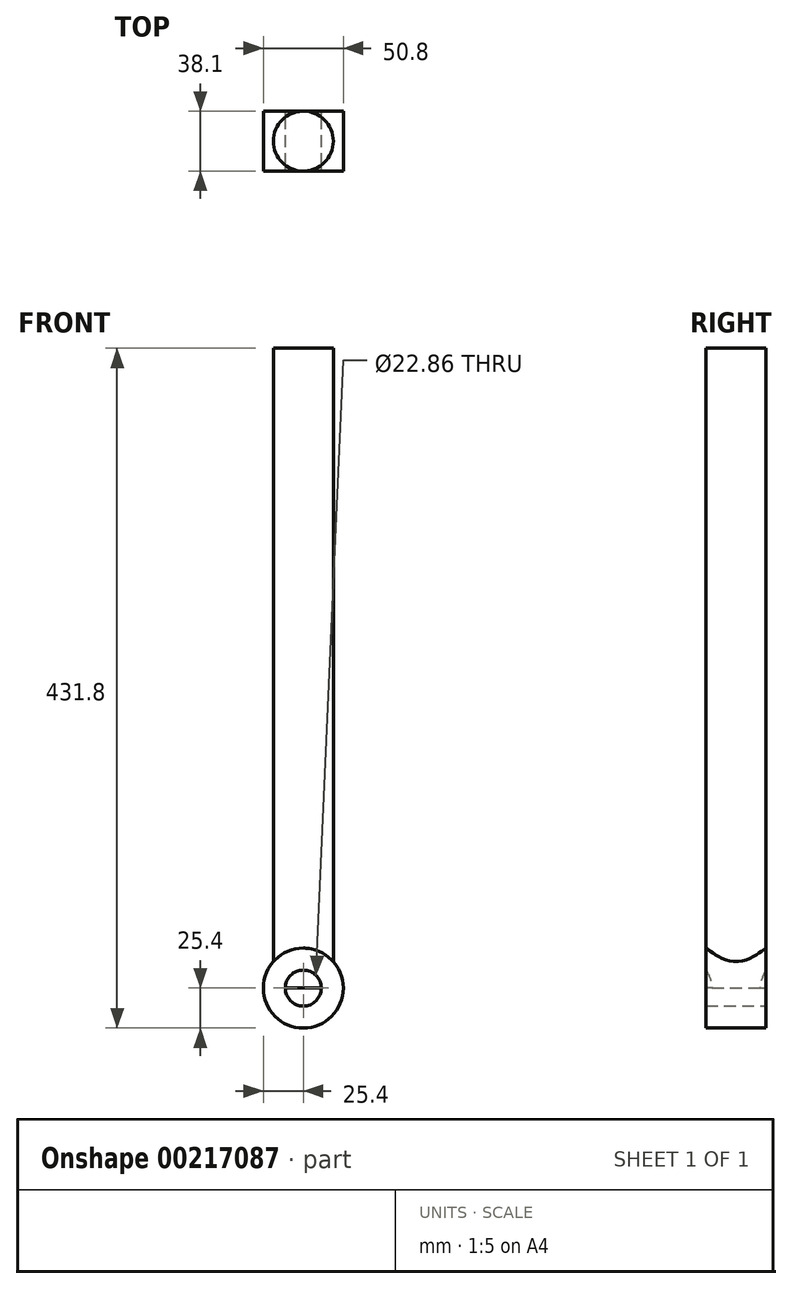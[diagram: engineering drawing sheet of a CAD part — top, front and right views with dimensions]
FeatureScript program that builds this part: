
annotation { "Feature Type Name" : "Feature", "Feature Type Description" : "" }
export const myFeature = defineFeature(function(context is Context, id is Id, definition is map)
    precondition{}
    {
        {
            var Q0;
            Q0=qCreatedBy(makeId("Top.planeOp"),FACE);
            var sketch = newSketch(context, id + "F0", { "sketchPlane" : qUnion([Q0])});
            skCircle(sketch, "E0", {"center": v(0, 0) * mm, "radius": 19.05 * mm});
            skSolve(sketch);
        }
        {
            var Q0;
            Q0=qCreatedBy(makeId("Front.planeOp"),FACE);
            var sketch = newSketch(context, id + "F1", { "sketchPlane" : qUnion([Q0])});
            skCircle(sketch, "E1", {"center": v(0, 0) * mm, "radius": 11.43 * mm});
            skCircle(sketch, "E2", {"center": v(0, 0) * mm, "radius": 25.4 * mm});
            skSolve(sketch);
        }
        {
            var Q0;
            Q0=makeQuery(id+"F1.imprint","IMPRINT",FACE,{"disambiguationData":[TD([[makeQuery(id+"F1.imprint","IMPRINT",EDGE,{"derivedFrom":sQuery(id+"F1.wireOp",EDGE,"E1")}),-1.0]])]});
            extrude(context, id + "F2", {"entities" : qUnion([Q0]), "depth" : 38.1 * mm, "symmetric" : true});
        }
        {
            var Q0;
            Q0=makeQuery(id+"F0.imprint","IMPRINT",FACE,{"disambiguationData":[TD([[makeQuery(id+"F0.imprint","IMPRINT",EDGE,{"derivedFrom":sQuery(id+"F0.wireOp",EDGE,"E0")}),1.0]])]});
            extrude(context, id + "F3", {"entities" : qUnion([Q0]), "operationType" : NewBodyOperationType.ADD, "depth" : 254 * mm});
        }
        {
            var Q0;
            Q0=makeQuery(id+"F3.opExtrude","CAP_FACE",FACE,{"disambiguationData":[OSD([sQuery(id+"F0.wireOp",EDGE,"E0")])],"isStart":false});
            var sketch = newSketch(context, id + "F4", { "sketchPlane" : qUnion([Q0])});
            skCircle(sketch, "E3", {"center": v(0, 0) * mm, "radius": 38.1 * mm});
            skSolve(sketch);
        }
        {
            var Q0;
            Q0=makeQuery(id+"F4.imprint","IMPRINT",FACE,{"disambiguationData":[TD([[makeQuery(id+"F4.imprint","IMPRINT",EDGE,{"derivedFrom":sQuery(id+"F4.wireOp",EDGE,"E3")}),1.0]])]});
            extrude(context, id + "F5", {"entities" : qUnion([Q0]), "depth" : 6.35 * mm});
        }
        {
            var Q0;
            Q0=makeQuery(id+"F3.opExtrude","CAP_FACE",FACE,{"disambiguationData":[OSD([sQuery(id+"F0.wireOp",EDGE,"E0")])],"isStart":false});
            extrude(context, id + "F6", {"entities" : qUnion([Q0]), "operationType" : NewBodyOperationType.ADD, "depth" : 152.4 * mm});
        }
        {
            var Q0;
            Q0=makeQuery(id+"F5.opExtrude","CAP_FACE",FACE,{"disambiguationData":[OSD([sQuery(id+"F0.wireOp",EDGE,"E0"),sQuery(id+"F4.wireOp",EDGE,"E3")])],"isStart":false});
            extrude(context, id + "F7", {"entities" : qUnion([Q0]), "operationType" : NewBodyOperationType.REMOVE, "oppositeDirection" : true, "depth" : 25.4 * mm});
        }
    });
